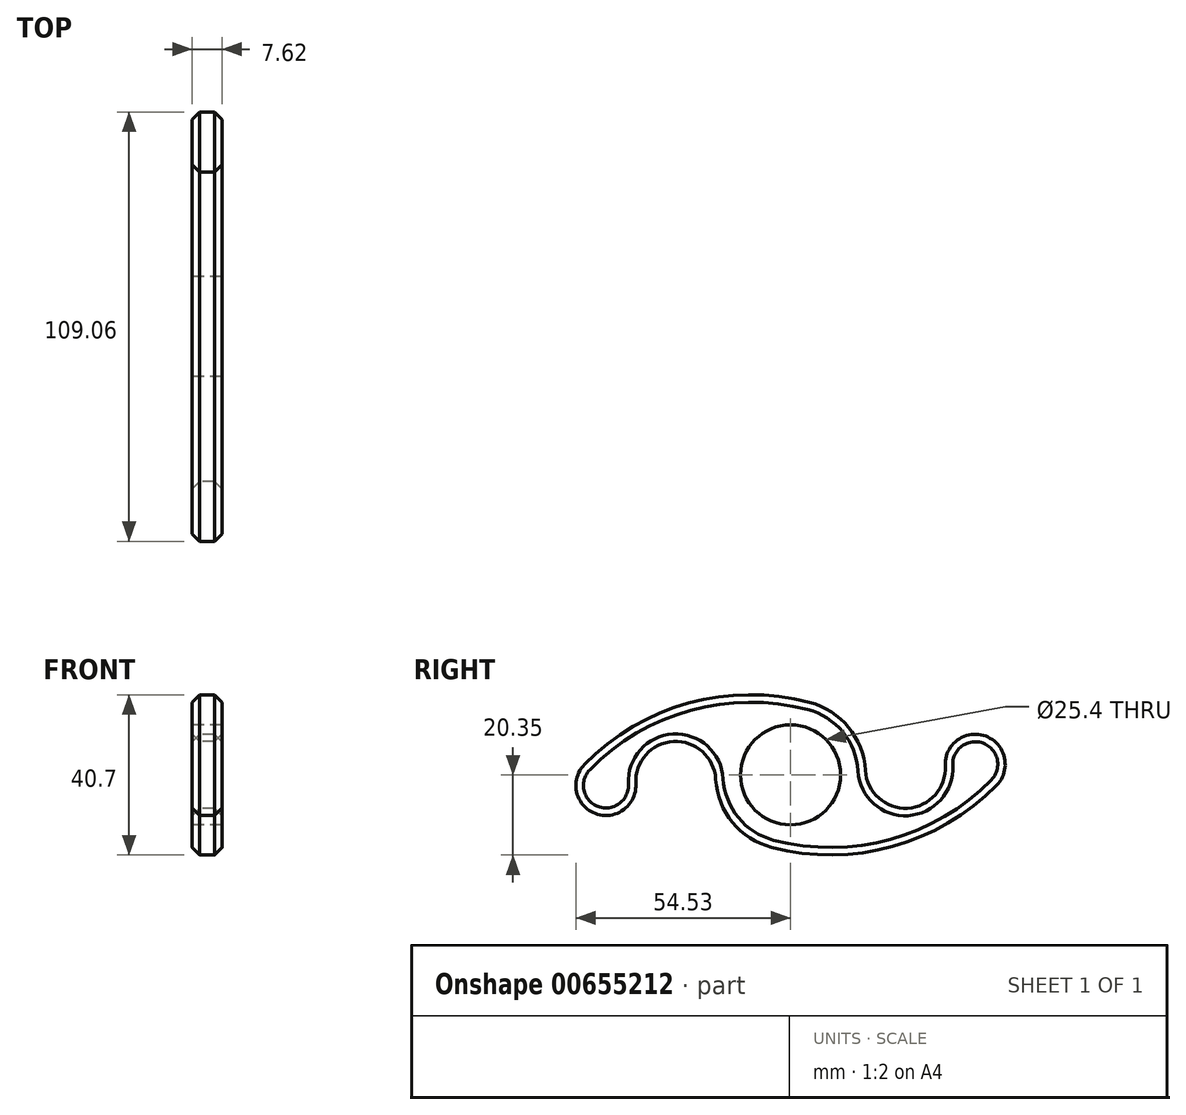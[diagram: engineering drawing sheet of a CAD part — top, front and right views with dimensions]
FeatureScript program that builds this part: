
annotation { "Feature Type Name" : "Feature", "Feature Type Description" : "" }
export const myFeature = defineFeature(function(context is Context, id is Id, definition is map)
    precondition{}
    {
        {
            var Q0;
            Q0=qCreatedBy(makeId("Right.planeOp"),FACE);
            var sketch = newSketch(context, id + "F0", { "sketchPlane" : qUnion([Q0])});
            skCircle(sketch, "E0", {"center": v(0, 0) * mm, "radius": 19.05 * mm});
            skCircle(sketch, "E1", {"center": v(0, 0) * mm, "radius": 12.7 * mm});
            skCircle(sketch, "E2", {"center": v(46.91, 2.7) * mm, "radius": 7.62 * mm});
            skArc(sketch, "E3", {"start": v(-4.82, -18.43) * mm, "mid": v(25.89, -18.22) * mm, "end": v(52.35, -2.64) * mm});
            skArc(sketch, "E4", {"start": v(19.02, 1.1) * mm, "mid": v(29.75, -8.47) * mm, "end": v(39.3, 2.26) * mm});
            skArc(sketch, "E5.1.0", {"start": v(-19.02, -1.1) * mm, "mid": v(-29.75, 8.47) * mm, "end": v(-39.3, -2.26) * mm});
            skArc(sketch, "E5.1.1", {"start": v(4.82, 18.43) * mm, "mid": v(-25.89, 18.22) * mm, "end": v(-52.35, 2.64) * mm});
            skCircle(sketch, "E5.1.2", {"center": v(-46.91, -2.7) * mm, "radius": 7.62 * mm});
            skSolve(sketch);
        }
        {
            var Q0;
            Q0 = qSketchRegion(id + "F0", true);
            extrude(context, id + "F1", {"entities" : qUnion([Q0]), "depth" : 7.62 * mm, "offsetDistance" : 25.4 * mm});
        }
        {
            var Q0;
            Q0=makeQuery(id+"F1.opExtrude","CAP_EDGE",EDGE,{"disambiguationData":[OSD([sQuery(id+"F0.wireOp",EDGE,"E3")])],"isStart":true});
            var Q1;
            Q1=makeQuery(id+"F1.opExtrude","CAP_EDGE",EDGE,{"disambiguationData":[OSD([sQuery(id+"F0.wireOp",EDGE,"E4")])],"isStart":true});
            var Q2;
            Q2=makeQuery(id+"F1.opExtrude","CAP_EDGE",EDGE,{"disambiguationData":[OSD([sQuery(id+"F0.wireOp",EDGE,"E3")])],"isStart":false});
            chamfer(context, id + "F2", {"entities" : qUnion([Q0, Q1, Q2]), "width" : 1.9 * mm, "tangentPropagation" : true});
        }
    });
